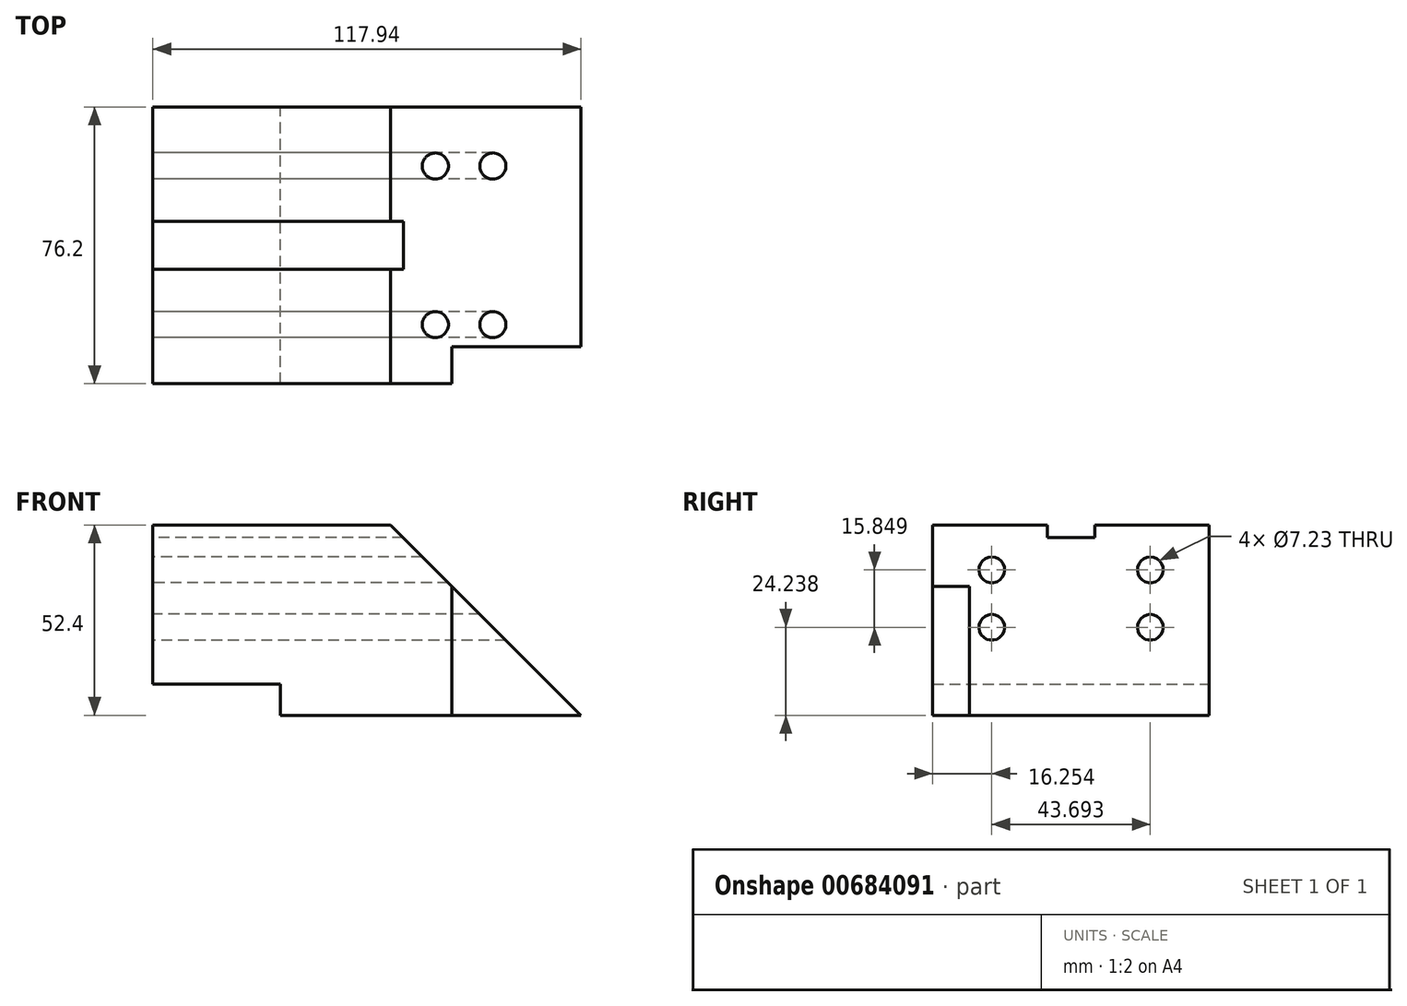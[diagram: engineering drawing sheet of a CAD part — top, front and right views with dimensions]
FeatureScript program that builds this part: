
annotation { "Feature Type Name" : "Feature", "Feature Type Description" : "" }
export const myFeature = defineFeature(function(context is Context, id is Id, definition is map)
    precondition{}
    {
        {
            var Q0;
            Q0=qCreatedBy(makeId("Front.planeOp"),FACE);
            var sketch = newSketch(context, id + "F0", { "sketchPlane" : qUnion([Q0])});
            skLineSegment(sketch, "E0", {"start": v(-65.54, 8.64) * mm, "end": v(-65.54, 52.4) * mm});
            skLineSegment(sketch, "E1", {"start": v(-65.54, 52.4) * mm, "end": v(0, 52.4) * mm});
            skLineSegment(sketch, "E2", {"start": v(0, 52.4) * mm, "end": v(52.4, 0) * mm});
            skLineSegment(sketch, "E3", {"start": v(52.4, 0) * mm, "end": v(-30.41, 0) * mm});
            skLineSegment(sketch, "E4", {"start": v(-30.41, 0) * mm, "end": v(-30.41, 8.64) * mm});
            skLineSegment(sketch, "E5", {"start": v(-30.41, 8.64) * mm, "end": v(-65.54, 8.64) * mm});
            skPoint(sketch, "E6.orphan", {"position": v(-65.54, 0) * mm});
            skSolve(sketch);
        }
        {
            var Q0;
            Q0 = qSketchRegion(id + "F0", true);
            extrude(context, id + "F1", {"entities" : qUnion([Q0]), "depth" : 38.1 * mm, "offsetDistance" : 25.4 * mm, "hasSecondDirection" : true, "secondDirectionOppositeDirection" : true, "secondDirectionDepth" : 38.1 * mm});
        }
        {
            var Q0;
            Q0=makeQuery(id+"F1.opExtrude","SWEPT_FACE",FACE,{"disambiguationData":[OSD([sQuery(id+"F0.wireOp",EDGE,"E0")])]});
            var sketch = newSketch(context, id + "F2", { "sketchPlane" : qUnion([Q0])});
            skLineSegment(sketch, "E7.bottom", {"start": v(6.57, 48.94) * mm, "end": v(-6.57, 48.94) * mm});
            skLineSegment(sketch, "E7.top", {"start": v(6.57, 55.87) * mm, "end": v(-6.57, 55.87) * mm});
            skLineSegment(sketch, "E7.left", {"start": v(6.57, 48.94) * mm, "end": v(6.57, 55.87) * mm});
            skLineSegment(sketch, "E7.right", {"start": v(-6.57, 48.94) * mm, "end": v(-6.57, 55.87) * mm});
            skPoint(sketch, "E7.middle", {"position": v(0, 52.4) * mm});
            skCircle(sketch, "E8", {"center": v(-21.85, 40.09) * mm, "radius": 3.62 * mm});
            skCircle(sketch, "E9", {"center": v(-21.85, 24.24) * mm, "radius": 3.62 * mm});
            skCircle(sketch, "E10.MirrorC", {"center": v(21.85, 24.24) * mm, "radius": 3.62 * mm});
            skCircle(sketch, "E11.MirrorC", {"center": v(21.85, 40.09) * mm, "radius": 3.62 * mm});
            skSolve(sketch);
        }
        {
            var Q0;
            Q0 = qSketchRegion(id + "F2", true);
            extrude(context, id + "F3", {"entities" : qUnion([Q0]), "operationType" : NewBodyOperationType.REMOVE, "endBound" : BoundingType.THROUGH_ALL, "oppositeDirection" : true, "depth" : 25.4 * mm, "offsetDistance" : 25.4 * mm});
        }
        {
            var Q0;
            Q0=makeQuery(id+"F1.opExtrude","SWEPT_FACE",FACE,{"disambiguationData":[OSD([sQuery(id+"F0.wireOp",EDGE,"E3")])]});
            var sketch = newSketch(context, id + "F4", { "sketchPlane" : qUnion([Q0])});
            skLineSegment(sketch, "E12.bottom", {"start": v(52.4, 38.1) * mm, "end": v(16.88, 38.1) * mm});
            skLineSegment(sketch, "E12.top", {"start": v(52.4, 27.98) * mm, "end": v(16.88, 27.98) * mm});
            skLineSegment(sketch, "E12.left", {"start": v(52.4, 38.1) * mm, "end": v(52.4, 27.98) * mm});
            skLineSegment(sketch, "E12.right", {"start": v(16.88, 38.1) * mm, "end": v(16.88, 27.98) * mm});
            skSolve(sketch);
        }
        {
            var Q0;
            Q0 = qSketchRegion(id + "F4", true);
            extrude(context, id + "F5", {"entities" : qUnion([Q0]), "operationType" : NewBodyOperationType.REMOVE, "endBound" : BoundingType.THROUGH_ALL, "oppositeDirection" : true, "depth" : 25.4 * mm, "offsetDistance" : 25.4 * mm});
        }
    });
